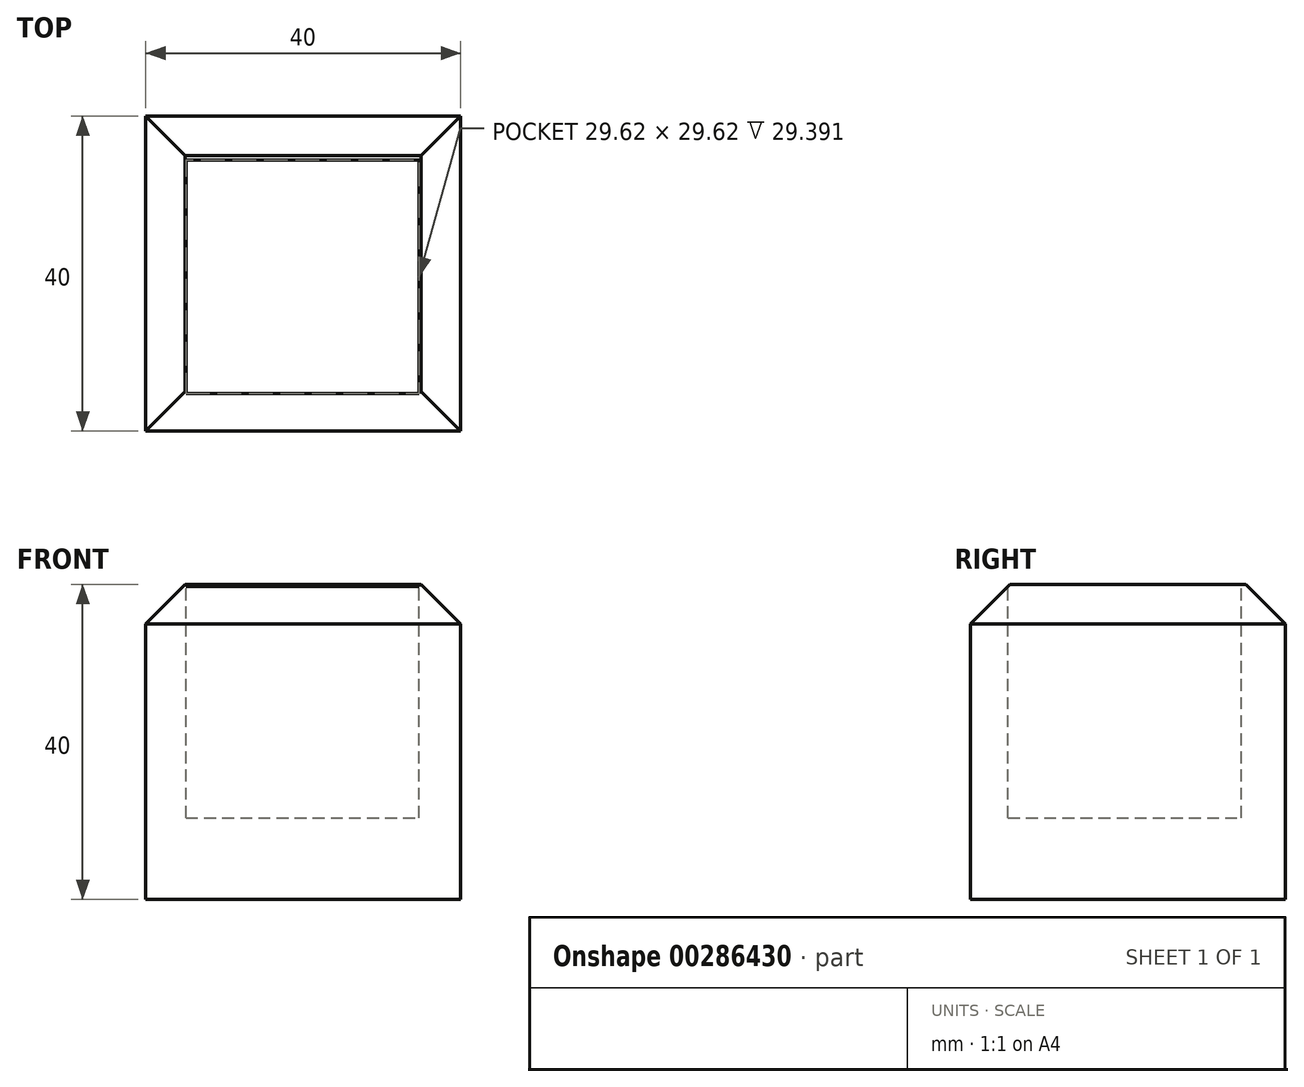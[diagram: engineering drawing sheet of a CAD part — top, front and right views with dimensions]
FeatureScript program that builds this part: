
annotation { "Feature Type Name" : "Feature", "Feature Type Description" : "" }
export const myFeature = defineFeature(function(context is Context, id is Id, definition is map)
    precondition{}
    {
        {
            var Q0;
            Q0=qCreatedBy(makeId("Top.planeOp"),FACE);
            var sketch = newSketch(context, id + "F0", { "sketchPlane" : qUnion([Q0])});
            skLineSegment(sketch, "E0.bottom", {"start": v(0, 0) * mm, "end": v(40, 0) * mm});
            skLineSegment(sketch, "E0.top", {"start": v(0, 40) * mm, "end": v(40, 40) * mm});
            skLineSegment(sketch, "E0.left", {"start": v(0, 0) * mm, "end": v(0, 40) * mm});
            skLineSegment(sketch, "E0.right", {"start": v(40, 0) * mm, "end": v(40, 40) * mm});
            skSolve(sketch);
        }
        {
            var Q0;
            Q0=makeQuery(id+"F0.imprint","IMPRINT",FACE,{"disambiguationData":[TD([[makeQuery(id+"F0.imprint","IMPRINT",EDGE,{"derivedFrom":sQuery(id+"F0.wireOp",EDGE,"E0.bottom")}),1.0]])]});
            extrude(context, id + "F1", {"entities" : qUnion([Q0]), "depth" : 40 * mm});
        }
        {
            var Q0;
            Q0=makeQuery(id+"F1.opExtrude","CAP_FACE",FACE,{"disambiguationData":[OSD([sQuery(id+"F0.wireOp",EDGE,"E0.bottom"),sQuery(id+"F0.wireOp",EDGE,"E0.top"),sQuery(id+"F0.wireOp",EDGE,"E0.left"),sQuery(id+"F0.wireOp",EDGE,"E0.right")])],"isStart":false});
            var sketch = newSketch(context, id + "F2", { "sketchPlane" : qUnion([Q0])});
            skLineSegment(sketch, "E1.bottom", {"start": v(5.11, 4.77) * mm, "end": v(34.73, 4.77) * mm});
            skLineSegment(sketch, "E1.top", {"start": v(5.11, 34.4) * mm, "end": v(34.73, 34.4) * mm});
            skLineSegment(sketch, "E1.left", {"start": v(5.11, 4.77) * mm, "end": v(5.11, 34.4) * mm});
            skLineSegment(sketch, "E1.right", {"start": v(34.73, 4.77) * mm, "end": v(34.73, 34.4) * mm});
            skSolve(sketch);
        }
        {
            var Q0;
            Q0=makeQuery(id+"F2.imprint","IMPRINT",FACE,{"disambiguationData":[TD([[makeQuery(id+"F2.imprint","IMPRINT",EDGE,{"derivedFrom":sQuery(id+"F2.wireOp",EDGE,"E1.bottom")}),1.0]])]});
            extrude(context, id + "F3", {"entities" : qUnion([Q0]), "operationType" : NewBodyOperationType.REMOVE, "oppositeDirection" : true, "depth" : 29.62 * mm});
        }
        {
            var Q0;
            Q0=makeQuery(id+"F1.opExtrude","CAP_EDGE",EDGE,{"disambiguationData":[OSD([sQuery(id+"F0.wireOp",EDGE,"E0.bottom")])],"isStart":false});
            var Q1;
            Q1=makeQuery(id+"F1.opExtrude","CAP_EDGE",EDGE,{"disambiguationData":[OSD([sQuery(id+"F0.wireOp",EDGE,"E0.right")])],"isStart":false});
            var Q2;
            Q2=makeQuery(id+"F1.opExtrude","CAP_EDGE",EDGE,{"disambiguationData":[OSD([sQuery(id+"F0.wireOp",EDGE,"E0.top")])],"isStart":false});
            var Q3;
            Q3=makeQuery(id+"F1.opExtrude","CAP_EDGE",EDGE,{"disambiguationData":[OSD([sQuery(id+"F0.wireOp",EDGE,"E0.left")])],"isStart":false});
            chamfer(context, id + "F4", {"entities" : qUnion([Q0, Q1, Q2, Q3]), "width" : 5 * mm, "tangentPropagation" : true});
        }
    });
